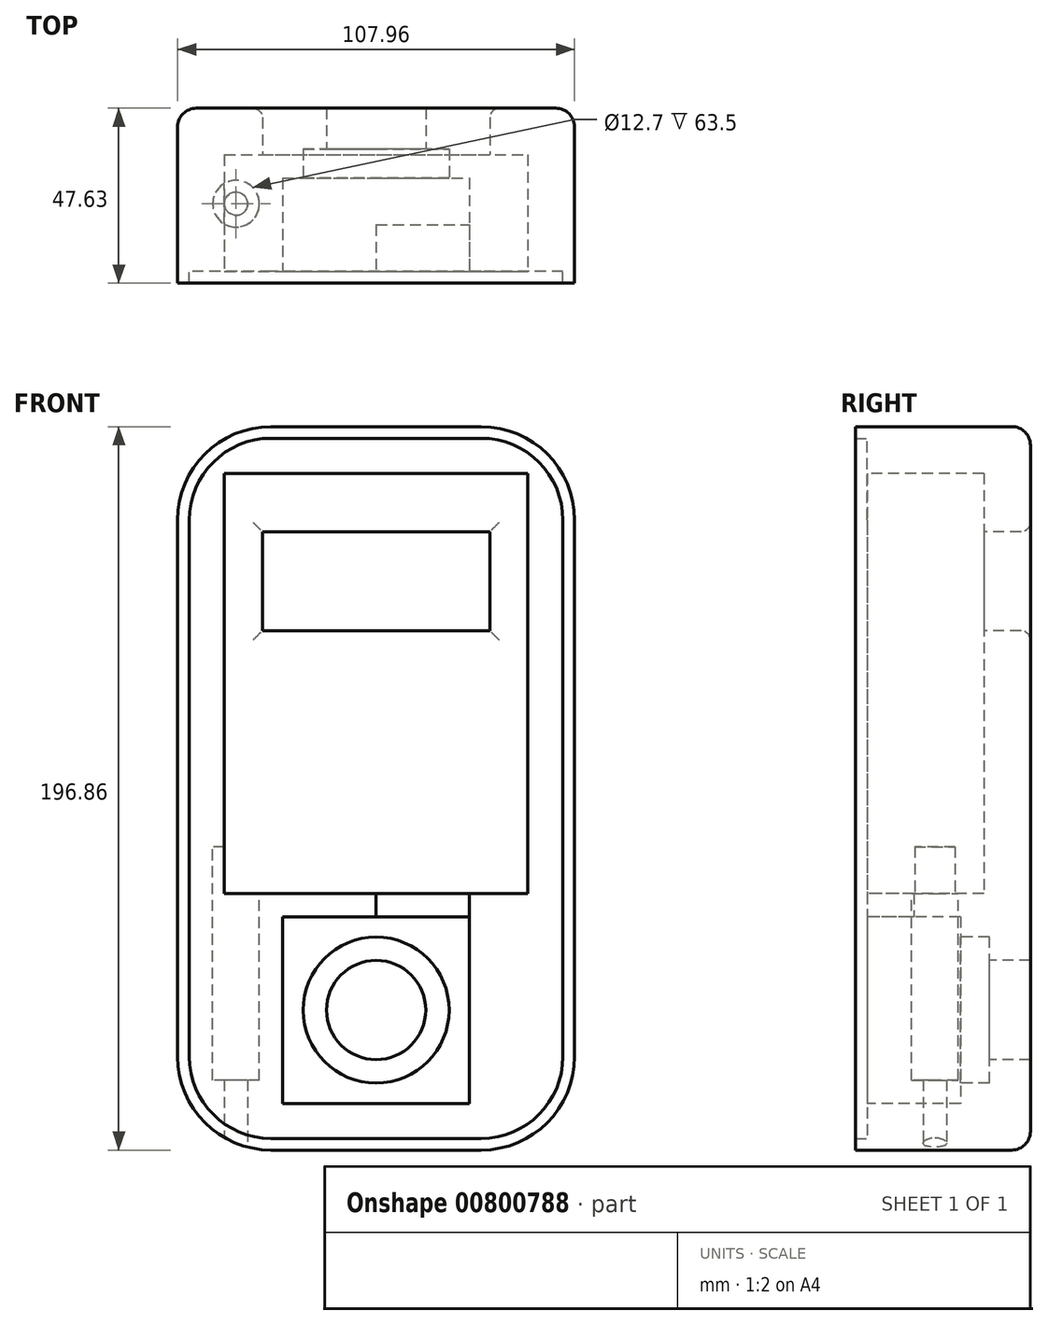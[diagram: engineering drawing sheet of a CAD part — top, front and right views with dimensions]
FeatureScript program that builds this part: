
annotation { "Feature Type Name" : "Feature", "Feature Type Description" : "" }
export const myFeature = defineFeature(function(context is Context, id is Id, definition is map)
    precondition{}
    {
        {
            var Q0;
            Q0=qCreatedBy(makeId("Front.planeOp"),FACE);
            var sketch = newSketch(context, id + "F0", { "sketchPlane" : qUnion([Q0])});
            skLineSegment(sketch, "E0.bottom", {"start": v(53.97, 98.43) * mm, "end": v(-53.98, 98.43) * mm});
            skLineSegment(sketch, "E0.top", {"start": v(53.98, -98.43) * mm, "end": v(-53.97, -98.43) * mm});
            skLineSegment(sketch, "E0.left", {"start": v(53.97, 98.43) * mm, "end": v(53.98, -98.43) * mm});
            skLineSegment(sketch, "E0.right", {"start": v(-53.98, 98.43) * mm, "end": v(-53.97, -98.43) * mm});
            skPoint(sketch, "E0.middle", {"position": v(0, 0) * mm});
            skSolve(sketch);
        }
        {
            var Q0;
            Q0 = qSketchRegion(id + "F0", true);
            extrude(context, id + "F1", {"entities" : qUnion([Q0]), "depth" : 44.45 * mm, "offsetDistance" : 25.4 * mm});
        }
        {
            var Q0;
            Q0=makeQuery(id+"F1.opExtrude","CAP_FACE",FACE,{"disambiguationData":[OSD([sQuery(id+"F0.wireOp",EDGE,"E0.bottom"),sQuery(id+"F0.wireOp",EDGE,"E0.top"),sQuery(id+"F0.wireOp",EDGE,"E0.left"),sQuery(id+"F0.wireOp",EDGE,"E0.right")])],"isStart":false});
            var sketch = newSketch(context, id + "F2", { "sketchPlane" : qUnion([Q0])});
            skLineSegment(sketch, "E1.bottom", {"start": v(-41.28, 85.72) * mm, "end": v(41.27, 85.73) * mm});
            skLineSegment(sketch, "E1.top", {"start": v(-41.27, -28.58) * mm, "end": v(41.27, -28.57) * mm});
            skLineSegment(sketch, "E1.left", {"start": v(-41.28, 85.72) * mm, "end": v(-41.27, -28.58) * mm});
            skLineSegment(sketch, "E1.right", {"start": v(41.28, 85.73) * mm, "end": v(41.28, -28.57) * mm});
            skSolve(sketch);
        }
        {
            var Q0;
            Q0 = qSketchRegion(id + "F2", true);
            extrude(context, id + "F3", {"entities" : qUnion([Q0]), "operationType" : NewBodyOperationType.REMOVE, "oppositeDirection" : true, "depth" : 31.75 * mm, "offsetDistance" : 25.4 * mm});
        }
        {
            var Q0;
            Q0=makeQuery(id+"F3.boolean.opBoolean","COPY",FACE,{"derivedFrom":makeQuery(id+"F3.opExtrude","CAP_FACE",FACE,{"disambiguationData":[OSD([sQuery(id+"F2.wireOp",EDGE,"E1.bottom"),sQuery(id+"F2.wireOp",EDGE,"E1.top"),sQuery(id+"F2.wireOp",EDGE,"E1.left"),sQuery(id+"F2.wireOp",EDGE,"E1.right")])],"isStart":false})});
            var sketch = newSketch(context, id + "F4", { "sketchPlane" : qUnion([Q0])});
            skLineSegment(sketch, "E2.bottom", {"start": v(-30.96, 69.85) * mm, "end": v(30.96, 69.85) * mm});
            skLineSegment(sketch, "E2.top", {"start": v(-30.96, 42.86) * mm, "end": v(30.96, 42.86) * mm});
            skLineSegment(sketch, "E2.left", {"start": v(-30.96, 69.85) * mm, "end": v(-30.96, 42.86) * mm});
            skLineSegment(sketch, "E2.right", {"start": v(30.96, 69.85) * mm, "end": v(30.96, 42.86) * mm});
            skSolve(sketch);
        }
        {
            var Q0;
            Q0 = qSketchRegion(id + "F4", true);
            extrude(context, id + "F5", {"entities" : qUnion([Q0]), "operationType" : NewBodyOperationType.REMOVE, "oppositeDirection" : true, "depth" : 25.4 * mm, "offsetDistance" : 25.4 * mm});
        }
        {
            var Q0;
            Q0=makeQuery(id+"F1.opExtrude","CAP_FACE",FACE,{"disambiguationData":[OSD([sQuery(id+"F0.wireOp",EDGE,"E0.bottom"),sQuery(id+"F0.wireOp",EDGE,"E0.top"),sQuery(id+"F0.wireOp",EDGE,"E0.left"),sQuery(id+"F0.wireOp",EDGE,"E0.right")])],"isStart":false});
            var sketch = newSketch(context, id + "F6", { "sketchPlane" : qUnion([Q0])});
            skLineSegment(sketch, "E3.bottom", {"start": v(-25.4, -34.93) * mm, "end": v(25.4, -34.92) * mm});
            skLineSegment(sketch, "E3.top", {"start": v(-25.4, -85.72) * mm, "end": v(25.4, -85.72) * mm});
            skLineSegment(sketch, "E3.left", {"start": v(-25.4, -34.93) * mm, "end": v(-25.4, -85.72) * mm});
            skLineSegment(sketch, "E3.right", {"start": v(25.4, -34.92) * mm, "end": v(25.4, -85.72) * mm});
            skSolve(sketch);
        }
        {
            var Q0;
            Q0 = qSketchRegion(id + "F6", true);
            extrude(context, id + "F7", {"entities" : qUnion([Q0]), "operationType" : NewBodyOperationType.REMOVE, "oppositeDirection" : true, "depth" : 25.4 * mm, "offsetDistance" : 25.4 * mm});
        }
        {
            var Q0;
            Q0=makeQuery(id+"F7.boolean.opBoolean","COPY",FACE,{"derivedFrom":makeQuery(id+"F7.opExtrude","CAP_FACE",FACE,{"disambiguationData":[OSD([sQuery(id+"F6.wireOp",EDGE,"E3.bottom"),sQuery(id+"F6.wireOp",EDGE,"E3.top"),sQuery(id+"F6.wireOp",EDGE,"E3.left"),sQuery(id+"F6.wireOp",EDGE,"E3.right")])],"isStart":false})});
            var sketch = newSketch(context, id + "F8", { "sketchPlane" : qUnion([Q0])});
            skCircle(sketch, "E4", {"center": v(0, -60.33) * mm, "radius": 19.84 * mm});
            skSolve(sketch);
        }
        {
            var Q0;
            Q0 = qSketchRegion(id + "F8", true);
            extrude(context, id + "F9", {"entities" : qUnion([Q0]), "operationType" : NewBodyOperationType.REMOVE, "oppositeDirection" : true, "depth" : 7.94 * mm, "offsetDistance" : 25.4 * mm});
        }
        {
            var Q0;
            Q0=makeQuery(id+"F9.boolean.opBoolean","COPY",FACE,{"derivedFrom":makeQuery(id+"F9.opExtrude","CAP_FACE",FACE,{"disambiguationData":[OSD([sQuery(id+"F8.wireOp",EDGE,"E4")])],"isStart":false})});
            var sketch = newSketch(context, id + "F10", { "sketchPlane" : qUnion([Q0])});
            skCircle(sketch, "E5", {"center": v(0, -60.33) * mm, "radius": 13.5 * mm});
            skSolve(sketch);
        }
        {
            var Q0;
            Q0 = qSketchRegion(id + "F10", true);
            extrude(context, id + "F11", {"entities" : qUnion([Q0]), "operationType" : NewBodyOperationType.REMOVE, "oppositeDirection" : true, "depth" : 25.4 * mm, "offsetDistance" : 25.4 * mm});
        }
        {
            var Q0;
            Q0=makeQuery(id+"F1.opExtrude","SWEPT_EDGE",EDGE,{"disambiguationData":[OSD([sQuery(id+"F0.wireOp",EDGE,"E0.bottom"),sQuery(id+"F0.wireOp",EDGE,"E0.left")])]});
            var Q1;
            Q1=makeQuery(id+"F1.opExtrude","SWEPT_EDGE",EDGE,{"disambiguationData":[OSD([sQuery(id+"F0.wireOp",EDGE,"E0.top"),sQuery(id+"F0.wireOp",EDGE,"E0.left")])]});
            var Q2;
            Q2=makeQuery(id+"F1.opExtrude","SWEPT_EDGE",EDGE,{"disambiguationData":[OSD([sQuery(id+"F0.wireOp",EDGE,"E0.top"),sQuery(id+"F0.wireOp",EDGE,"E0.right")])]});
            var Q3;
            Q3=makeQuery(id+"F1.opExtrude","SWEPT_EDGE",EDGE,{"disambiguationData":[OSD([sQuery(id+"F0.wireOp",EDGE,"E0.bottom"),sQuery(id+"F0.wireOp",EDGE,"E0.right")])]});
            fillet(context, id + "F12", {"entities" : qUnion([Q0, Q1, Q2, Q3]), "radius" : 25.4 * mm, "tangentPropagation" : true, "allowEdgeOverflow" : false});
        }
        {
            var Q0;
            Q0=makeQuery(id+"F1.opExtrude","CAP_EDGE",EDGE,{"disambiguationData":[OSD([sQuery(id+"F0.wireOp",EDGE,"E0.right")])],"isStart":true});
            var Q1;
            {var subQ0=sQuery(id+"F0.wireOp",EDGE,"E0.right");var subQ1=sQuery(id+"F0.wireOp",EDGE,"E0.top");Q1=makeQuery(id+"F12.opFillet","BLEND_EDGE",EDGE,{"blendedFrom":[makeQuery(id+"F1.opExtrude","SWEPT_EDGE",EDGE,{"disambiguationData":[OSD([subQ1,subQ0])]}),makeQuery(id+"F1.opExtrude","CAP_FACE",FACE,{"disambiguationData":[OSD([sQuery(id+"F0.wireOp",EDGE,"E0.bottom"),subQ1,sQuery(id+"F0.wireOp",EDGE,"E0.left"),subQ0])],"isStart":true})],"blendedInto":[makeQuery(id+"F1.opExtrude","CAP_FACE",FACE,{"disambiguationData":[OSD([sQuery(id+"F0.wireOp",EDGE,"E0.bottom"),subQ1,sQuery(id+"F0.wireOp",EDGE,"E0.left"),subQ0])],"isStart":true})]});}
            var Q2;
            Q2=makeQuery(id+"F1.opExtrude","CAP_EDGE",EDGE,{"disambiguationData":[OSD([sQuery(id+"F0.wireOp",EDGE,"E0.top")])],"isStart":true});
            fillet(context, id + "F13", {"entities" : qUnion([Q0, Q1, Q2]), "radius" : 5.08 * mm, "tangentPropagation" : true, "allowEdgeOverflow" : false});
        }
        {
            var Q0;
            Q0=makeQuery(id+"F5.boolean.opBoolean","INTERSECT",EDGE,{"derivedFrom":[makeQuery(id+"F1.opExtrude","CAP_FACE",FACE,{"disambiguationData":[OSD([sQuery(id+"F0.wireOp",EDGE,"E0.bottom"),sQuery(id+"F0.wireOp",EDGE,"E0.top"),sQuery(id+"F0.wireOp",EDGE,"E0.left"),sQuery(id+"F0.wireOp",EDGE,"E0.right")])],"isStart":true}),makeQuery(id+"F5.opExtrude","SWEPT_FACE",FACE,{"disambiguationData":[OSD([sQuery(id+"F4.wireOp",EDGE,"E2.bottom")])]})]});
            var Q1;
            Q1=makeQuery(id+"F5.boolean.opBoolean","INTERSECT",EDGE,{"derivedFrom":[makeQuery(id+"F1.opExtrude","CAP_FACE",FACE,{"disambiguationData":[OSD([sQuery(id+"F0.wireOp",EDGE,"E0.bottom"),sQuery(id+"F0.wireOp",EDGE,"E0.top"),sQuery(id+"F0.wireOp",EDGE,"E0.left"),sQuery(id+"F0.wireOp",EDGE,"E0.right")])],"isStart":true}),makeQuery(id+"F5.opExtrude","SWEPT_FACE",FACE,{"disambiguationData":[OSD([sQuery(id+"F4.wireOp",EDGE,"E2.right")])]})]});
            var Q2;
            Q2=makeQuery(id+"F5.boolean.opBoolean","INTERSECT",EDGE,{"derivedFrom":[makeQuery(id+"F1.opExtrude","CAP_FACE",FACE,{"disambiguationData":[OSD([sQuery(id+"F0.wireOp",EDGE,"E0.bottom"),sQuery(id+"F0.wireOp",EDGE,"E0.top"),sQuery(id+"F0.wireOp",EDGE,"E0.left"),sQuery(id+"F0.wireOp",EDGE,"E0.right")])],"isStart":true}),makeQuery(id+"F5.opExtrude","SWEPT_FACE",FACE,{"disambiguationData":[OSD([sQuery(id+"F4.wireOp",EDGE,"E2.top")])]})]});
            var Q3;
            Q3=makeQuery(id+"F5.boolean.opBoolean","INTERSECT",EDGE,{"derivedFrom":[makeQuery(id+"F1.opExtrude","CAP_FACE",FACE,{"disambiguationData":[OSD([sQuery(id+"F0.wireOp",EDGE,"E0.bottom"),sQuery(id+"F0.wireOp",EDGE,"E0.top"),sQuery(id+"F0.wireOp",EDGE,"E0.left"),sQuery(id+"F0.wireOp",EDGE,"E0.right")])],"isStart":true}),makeQuery(id+"F5.opExtrude","SWEPT_FACE",FACE,{"disambiguationData":[OSD([sQuery(id+"F4.wireOp",EDGE,"E2.left")])]})]});
            fillet(context, id + "F14", {"entities" : qUnion([Q0, Q1, Q2, Q3]), "radius" : 2.54 * mm, "tangentPropagation" : true, "allowEdgeOverflow" : false});
        }
        {
            var Q0;
            Q0=makeQuery(id+"F1.opExtrude","CAP_FACE",FACE,{"disambiguationData":[OSD([sQuery(id+"F0.wireOp",EDGE,"E0.bottom"),sQuery(id+"F0.wireOp",EDGE,"E0.top"),sQuery(id+"F0.wireOp",EDGE,"E0.left"),sQuery(id+"F0.wireOp",EDGE,"E0.right")])],"isStart":false});
            var sketch = newSketch(context, id + "F15", { "sketchPlane" : qUnion([Q0])});
            skArc(sketch, "E6.0", {"start": v(50.8, 73.03) * mm, "mid": v(44.3, 88.74) * mm, "end": v(28.57, 95.25) * mm});
            skLineSegment(sketch, "E6.1", {"start": v(50.8, 73.03) * mm, "end": v(50.8, -73.03) * mm});
            skLineSegment(sketch, "E6.2", {"start": v(28.57, 95.25) * mm, "end": v(-28.58, 95.25) * mm});
            skArc(sketch, "E6.3", {"start": v(28.58, -95.25) * mm, "mid": v(44.3, -88.74) * mm, "end": v(50.8, -73.03) * mm});
            skArc(sketch, "E6.4", {"start": v(-28.58, 95.25) * mm, "mid": v(-44.3, 88.74) * mm, "end": v(-50.8, 73.03) * mm});
            skLineSegment(sketch, "E6.5", {"start": v(-50.8, 73.03) * mm, "end": v(-50.8, -73.03) * mm});
            skArc(sketch, "E6.6", {"start": v(-50.8, -73.03) * mm, "mid": v(-44.3, -88.74) * mm, "end": v(-28.57, -95.25) * mm});
            skLineSegment(sketch, "E6.7", {"start": v(28.58, -95.25) * mm, "end": v(-28.57, -95.25) * mm});
            skLineSegment(sketch, "E7.0", {"start": v(28.57, 98.43) * mm, "end": v(-28.58, 98.43) * mm});
            skArc(sketch, "E7.1", {"start": v(53.97, 73.03) * mm, "mid": v(46.54, 90.99) * mm, "end": v(28.57, 98.43) * mm});
            skArc(sketch, "E7.2", {"start": v(-28.58, 98.43) * mm, "mid": v(-46.54, 90.99) * mm, "end": v(-53.98, 73.03) * mm});
            skLineSegment(sketch, "E7.3", {"start": v(53.97, 73.03) * mm, "end": v(53.98, -73.03) * mm});
            skLineSegment(sketch, "E7.4", {"start": v(-53.98, 73.03) * mm, "end": v(-53.97, -73.03) * mm});
            skArc(sketch, "E7.5", {"start": v(-53.97, -73.03) * mm, "mid": v(-46.54, -90.99) * mm, "end": v(-28.57, -98.43) * mm});
            skLineSegment(sketch, "E7.6", {"start": v(28.58, -98.43) * mm, "end": v(-28.57, -98.43) * mm});
            skArc(sketch, "E7.7", {"start": v(28.58, -98.43) * mm, "mid": v(46.54, -90.99) * mm, "end": v(53.98, -73.03) * mm});
            skSolve(sketch);
        }
        {
            var Q0;
            Q0 = qSketchRegion(id + "F15", true);
            extrude(context, id + "F16", {"entities" : qUnion([Q0]), "operationType" : NewBodyOperationType.ADD, "depth" : 3.17 * mm, "offsetDistance" : 25.4 * mm});
        }
        {
            var Q0;
            Q0=makeQuery(id+"F16.boolean.opBoolean","MERGE",FACE,{"derivedFrom":[makeQuery(id+"F1.opExtrude","SWEPT_FACE",FACE,{"disambiguationData":[OSD([sQuery(id+"F0.wireOp",EDGE,"E0.top")])]}),makeQuery(id+"F16.opExtrude","SWEPT_FACE",FACE,{"disambiguationData":[OSD([sQuery(id+"F15.wireOp",EDGE,"E7.6")])]})]});
            var sketch = newSketch(context, id + "F17", { "sketchPlane" : qUnion([Q0])});
            skCircle(sketch, "E8", {"center": v(-38.1, 25.99) * mm, "radius": 3.18 * mm});
            skSolve(sketch);
        }
        {
            var Q0;
            Q0 = qSketchRegion(id + "F17", true);
            extrude(context, id + "F18", {"entities" : qUnion([Q0]), "operationType" : NewBodyOperationType.REMOVE, "oppositeDirection" : true, "depth" : 76.2 * mm, "offsetDistance" : 25.4 * mm});
        }
        {
            var Q0;
            Q0=makeQuery(id+"F3.boolean.opBoolean","COPY",FACE,{"derivedFrom":makeQuery(id+"F3.opExtrude","SWEPT_FACE",FACE,{"disambiguationData":[OSD([sQuery(id+"F2.wireOp",EDGE,"E1.top")])]})});
            var sketch = newSketch(context, id + "F19", { "sketchPlane" : qUnion([Q0])});
            skCircle(sketch, "E9.0", {"center": v(-38.1, -25.99) * mm, "radius": 6.35 * mm});
            skSolve(sketch);
        }
        {
            var Q0;
            Q0 = qSketchRegion(id + "F19", true);
            extrude(context, id + "F20", {"entities" : qUnion([Q0]), "operationType" : NewBodyOperationType.REMOVE, "oppositeDirection" : true, "depth" : 50.8 * mm, "offsetDistance" : 25.4 * mm});
        }
        {
            var Q0;
            Q0 = qSketchRegion(id + "F19", true);
            extrude(context, id + "F21", {"entities" : qUnion([Q0]), "operationType" : NewBodyOperationType.REMOVE, "depth" : 12.7 * mm, "offsetDistance" : 25.4 * mm});
        }
        {
            var Q0;
            Q0=makeQuery(id+"F1.opExtrude","CAP_FACE",FACE,{"disambiguationData":[OSD([sQuery(id+"F0.wireOp",EDGE,"E0.bottom"),sQuery(id+"F0.wireOp",EDGE,"E0.top"),sQuery(id+"F0.wireOp",EDGE,"E0.left"),sQuery(id+"F0.wireOp",EDGE,"E0.right")])],"isStart":false});
            var sketch = newSketch(context, id + "F22", { "sketchPlane" : qUnion([Q0])});
            skLineSegment(sketch, "E10.bottom", {"start": v(0, -28.58) * mm, "end": v(25.4, -28.58) * mm});
            skLineSegment(sketch, "E10.top", {"start": v(0, -34.93) * mm, "end": v(25.4, -34.93) * mm});
            skLineSegment(sketch, "E10.left", {"start": v(0, -28.58) * mm, "end": v(0, -34.93) * mm});
            skLineSegment(sketch, "E10.right", {"start": v(25.4, -28.58) * mm, "end": v(25.4, -34.93) * mm});
            skSolve(sketch);
        }
        {
            var Q0;
            Q0 = qSketchRegion(id + "F22", true);
            extrude(context, id + "F23", {"entities" : qUnion([Q0]), "operationType" : NewBodyOperationType.REMOVE, "oppositeDirection" : true, "depth" : 12.7 * mm, "offsetDistance" : 25.4 * mm});
        }
    });
